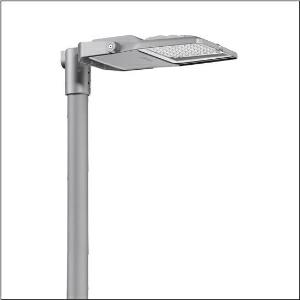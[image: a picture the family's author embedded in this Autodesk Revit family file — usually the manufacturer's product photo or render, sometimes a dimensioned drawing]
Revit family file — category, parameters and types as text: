
# Revit family: floodlight_fl_21_iq_mini___pl64_5xa7771c2e3a_b06c
name_source: partatom
category: Lighting Fixtures
units: mm (PartAtom-declared; Revit-internal decimal feet)

## family parameters
Cut with Voids When Loaded = No
Host = Face
Light Source = No
Part Type = Normal
Room Calculation Point = No
Round Connector Dimension = Use Diameter
Shared = No

## types (1)
- --- (1 x LED, 11790 lm, 87.2 W, 3000K)
    Apparent Load = 87 VA
    CIE Flux Codes = 28 80 98 100 100
    Color Rendering = 70
    Color Temperature = 3000K
    Default Elevation = 1800 mm
    Description = Floodlight FL 21 iQ mini, floodlight, primary light control with lens, of PMMA, primary optical cover: protective disc, of toughened safety glass, transparent, light distribution: PL64, light emission: direct distribution, installation type: surface-mounted, LED, High Power LED, rated luminous flux: 11.790lm, luminous efficacy: 135lm/W, light colour: 730, colour temperature: 3000K, control: Auto-Match, Temp-Guard, Lumen-Switch, Night-Set, Smart-Wire, Light-Fading, Desk-Remote (wireless, voltage-free reading and setting of iQ features in the workshop via application-optimized NFC function/RFID function), optimised constant luminous flux control (CLO 2.0), with terminal, 6-pole, mains connection: 220..240V, AC, 50/60Hz, start of lifetime: 87W, end of service life: 92W, reduction: 40W, luminaire housing, of diecast aluminium, powder-coated, Siteco® metallic grey (DB 702S), corrosivity category C5 mid according to DIN EN ISO 12944, sealing non-destructively replaceable, please order mast flange separately, mast bracket, of steel, galvanised, powder-coated, Siteco® metallic grey (DB 702S), protection rating (complete): IP66, insulation class (complete): insulation class II (safety insulation), certification: CE, ENEC, VDE, protection symbol: D, impact resistance: IK08, permissible operating ambient temperature: -40..+40°C, permissible operating ambient temperature for outdoor applications: -40..+50°C, standard: DIN EN 12944, LABS conformity tested according to VDMA 24364:2018-05, packaging unit: 1 piece

Light Distribution: PL64
    Height = 70 mm
    Lamp = 1 x LED
    Lamp Light Flux = 11790 lm
    Lamp Power = 87.2 W
    Lamp count = 1
    Length = 485 mm
    Luminous efficacy = 135 lm/W
    Manufacturer = Siteco
    ModVariant = No
    Model = 5XA7771C2E3A
    Number of Poles = 1
    OnlyDefault = Yes
    Power Factor = 1
    Product Name = Floodlight FL 21 iQ mini | PL64
    Product group = floodlight | pylon annexe
    ProductGroupID = 6200
    Protection Class = Protection class II
    Protection Degree = IP 66
    RLX_Detail_Level = 1
    RLX_Emergency_Light_Flux = 0 lm
    RLX_Emergency_Type = 0
    RLX_Emergency_Type_DB = No
    RlxData = <blob elided: 101385 chars, md5=27bf5e08>
    Socket = socket
    Standby Power = 0 W
    System Light Flux = 11790 lm
    System Power = 87 W
    Type Comments = factory setting: luminous flux: 100 % | dim-lin: 254 | 456 mA
    Type Image = l_1007125.jpg
    URL = http://relux.com
    VarID = @adj_116765
    Voltage = 0 V
    Weight = 0.00 kg
    Width = 337 mm

## geometry (parser evidence)
native form markers: Blend x4, Sweep x12
no freeform markers — native parametric forms only
